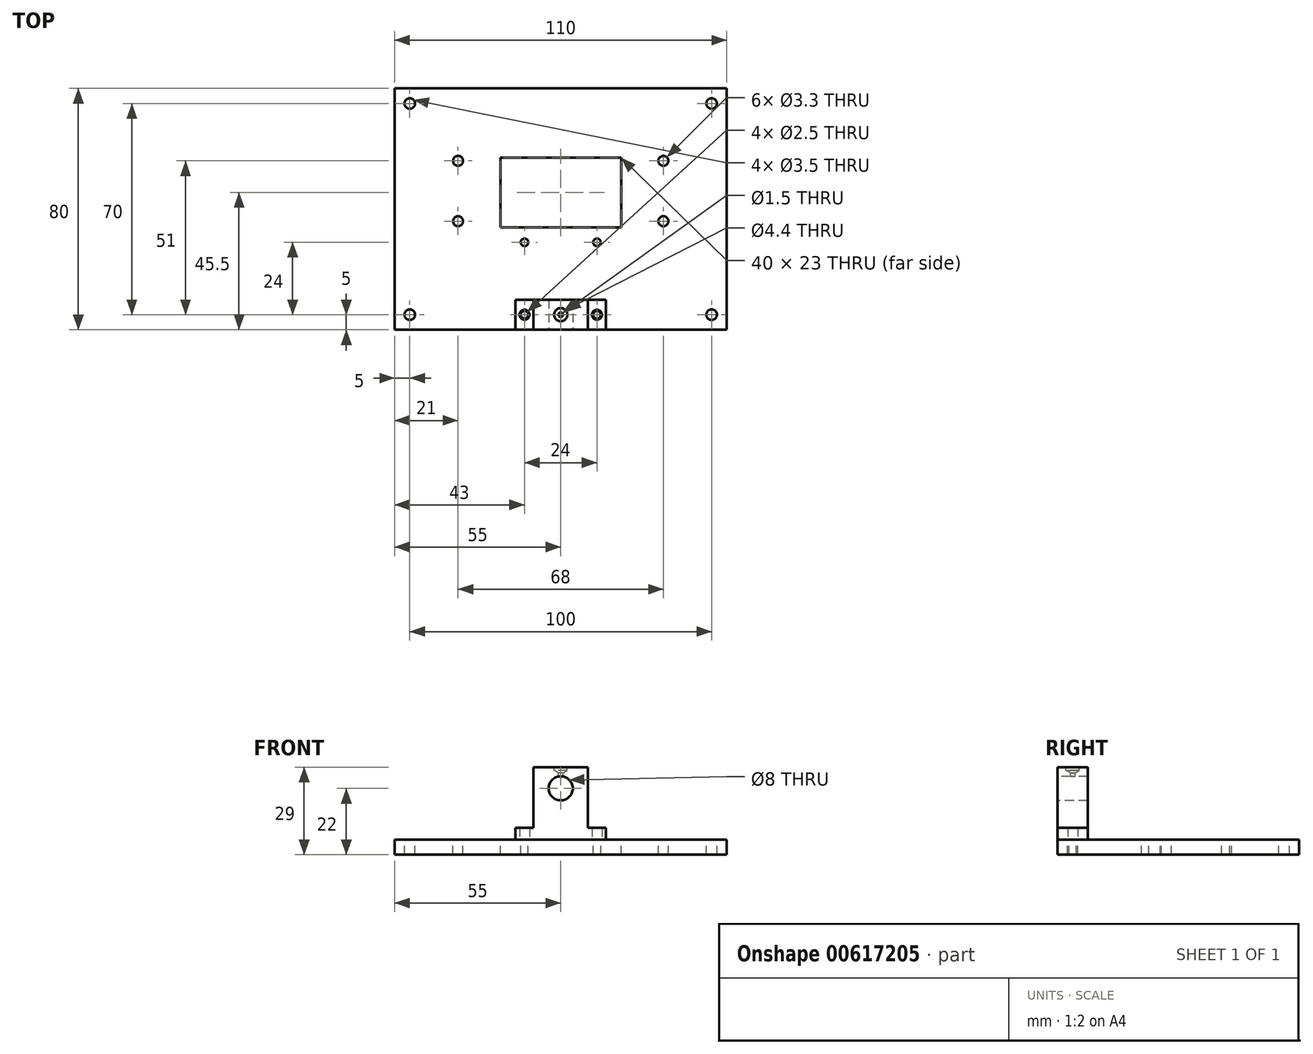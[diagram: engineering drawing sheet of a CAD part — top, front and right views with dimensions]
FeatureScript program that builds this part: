
annotation { "Feature Type Name" : "Feature", "Feature Type Description" : "" }
export const myFeature = defineFeature(function(context is Context, id is Id, definition is map)
    precondition{}
    {
        {
            var Q0;
            Q0=qCreatedBy(makeId("Top.planeOp"),FACE);
            var sketch = newSketch(context, id + "F0", { "sketchPlane" : qUnion([Q0])});
            skLineSegment(sketch, "E0.bottom", {"start": v(-55, 80) * mm, "end": v(55, 80) * mm});
            skLineSegment(sketch, "E0.top", {"start": v(-55, 0) * mm, "end": v(55, 0) * mm});
            skLineSegment(sketch, "E0.left", {"start": v(-55, 80) * mm, "end": v(-55, 0) * mm});
            skLineSegment(sketch, "E0.right", {"start": v(55, 80) * mm, "end": v(55, 0) * mm});
            skSolve(sketch);
        }
        {
            var Q0;
            Q0 = qSketchRegion(id + "F0", true);
            extrude(context, id + "F1", {"entities" : qUnion([Q0]), "oppositeDirection" : true, "depth" : 5 * mm, "offsetDistance" : 25 * mm});
        }
        {
            var Q0;
            Q0=makeQuery(id+"F1.opExtrude","CAP_FACE",FACE,{"disambiguationData":[OSD([sQuery(id+"F0.wireOp",EDGE,"E0.bottom"),sQuery(id+"F0.wireOp",EDGE,"E0.top"),sQuery(id+"F0.wireOp",EDGE,"E0.left"),sQuery(id+"F0.wireOp",EDGE,"E0.right")])],"isStart":true});
            var sketch = newSketch(context, id + "F2", { "sketchPlane" : qUnion([Q0])});
            skLineSegment(sketch, "E1.bottom", {"start": v(20, 34) * mm, "end": v(-20, 34) * mm});
            skLineSegment(sketch, "E1.top", {"start": v(20, 57) * mm, "end": v(-20, 57) * mm});
            skLineSegment(sketch, "E1.left", {"start": v(20, 34) * mm, "end": v(20, 57) * mm});
            skLineSegment(sketch, "E1.right", {"start": v(-20, 34) * mm, "end": v(-20, 57) * mm});
            skPoint(sketch, "E1.middle", {"position": v(0, 45.5) * mm});
            skSolve(sketch);
        }
        {
            var Q0;
            Q0 = qSketchRegion(id + "F2", true);
            extrude(context, id + "F3", {"entities" : qUnion([Q0]), "operationType" : NewBodyOperationType.REMOVE, "endBound" : BoundingType.THROUGH_ALL, "oppositeDirection" : true, "depth" : 25 * mm, "offsetDistance" : 25 * mm});
        }
        {
            var Q0;
            Q0=makeQuery(id+"F1.opExtrude","CAP_FACE",FACE,{"disambiguationData":[OSD([sQuery(id+"F0.wireOp",EDGE,"E0.bottom"),sQuery(id+"F0.wireOp",EDGE,"E0.top"),sQuery(id+"F0.wireOp",EDGE,"E0.left"),sQuery(id+"F0.wireOp",EDGE,"E0.right")])],"isStart":true});
            var sketch = newSketch(context, id + "F4", { "sketchPlane" : qUnion([Q0])});
            skLineSegment(sketch, "E2.bottom", {"start": v(12, 5) * mm, "end": v(-12, 5) * mm, "construction": true});
            skLineSegment(sketch, "E2.top", {"start": v(12, 29) * mm, "end": v(-12, 29) * mm, "construction": true});
            skLineSegment(sketch, "E2.left", {"start": v(12, 5) * mm, "end": v(12, 29) * mm, "construction": true});
            skLineSegment(sketch, "E2.right", {"start": v(-12, 5) * mm, "end": v(-12, 29) * mm, "construction": true});
            skPoint(sketch, "E2.middle", {"position": v(0, 17) * mm});
            skLineSegment(sketch, "E3.bottom", {"start": v(34, 36) * mm, "end": v(-34, 36) * mm, "construction": true});
            skLineSegment(sketch, "E3.top", {"start": v(34, 56) * mm, "end": v(-34, 56) * mm, "construction": true});
            skLineSegment(sketch, "E3.left", {"start": v(34, 36) * mm, "end": v(34, 56) * mm, "construction": true});
            skLineSegment(sketch, "E3.right", {"start": v(-34, 36) * mm, "end": v(-34, 56) * mm, "construction": true});
            skPoint(sketch, "E3.middle", {"position": v(0, 46) * mm});
            skSolve(sketch);
        }
        {
            var Q0;
            Q0=sQuery(id+"F4.wireOp",VERTEX,"E2.right.start");
            var Q1;
            Q1=sQuery(id+"F4.wireOp",VERTEX,"E2.bottom.start");
            var Q2;
            Q2=sQuery(id+"F4.wireOp",VERTEX,"E2.left.end");
            var Q3;
            Q3=sQuery(id+"F4.wireOp",VERTEX,"E2.right.end");
            var Q4;
            Q4=makeQuery(id+"F1.opExtrude","SWEPT_BODY",BODY,{"disambiguationData":[OSD([sQuery(id+"F0.wireOp",EDGE,"E0.bottom"),sQuery(id+"F0.wireOp",EDGE,"E0.top"),sQuery(id+"F0.wireOp",EDGE,"E0.left"),sQuery(id+"F0.wireOp",EDGE,"E0.right")])]});
            hole(context, id + "F5", {"style" : HoleStyle.SIMPLE, "endStyle" : HoleEndStyle.THROUGH, "standardTappedOrClearance" : lookupTablePath({ "standard" : "ISO", "engagement" : "75%", "pitch" : "0.5 mm", "size" : "M3", "type" : "Tapped" }), "standardBlindInLast" : lookupTablePath({ "standard" : "ISO", "engagement" : "75%", "pitch" : "0.5 mm", "size" : "M3", "type" : "Tapped" }), "holeDiameter" : 2.5 * mm, "majorDiameter" : 3 * mm, "showTappedDepth" : true, "isTappedThrough" : true, "tappedDepth" : 12 * mm, "tapClearance" : 3, "locations" : qUnion([Q0, Q1, Q2, Q3]), "scope" : qUnion([Q4])});
        }
        {
            var Q0;
            Q0=sQuery(id+"F4.wireOp",VERTEX,"E3.right.start");
            var Q1;
            Q1=sQuery(id+"F4.wireOp",VERTEX,"E3.left.start");
            var Q2;
            Q2=sQuery(id+"F4.wireOp",VERTEX,"E3.left.end");
            var Q3;
            Q3=sQuery(id+"F4.wireOp",VERTEX,"E3.top.end");
            var Q4;
            Q4=makeQuery(id+"F1.opExtrude","SWEPT_BODY",BODY,{"disambiguationData":[OSD([sQuery(id+"F0.wireOp",EDGE,"E0.bottom"),sQuery(id+"F0.wireOp",EDGE,"E0.top"),sQuery(id+"F0.wireOp",EDGE,"E0.left"),sQuery(id+"F0.wireOp",EDGE,"E0.right")])]});
            hole(context, id + "F6", {"style" : HoleStyle.SIMPLE, "endStyle" : HoleEndStyle.THROUGH, "standardTappedOrClearance" : lookupTablePath({ "standard" : "ISO", "engagement" : "75%", "pitch" : "0.7 mm", "size" : "M4", "type" : "Tapped" }), "standardBlindInLast" : lookupTablePath({ "standard" : "ISO", "engagement" : "75%", "pitch" : "0.7 mm", "size" : "M4", "type" : "Tapped" }), "holeDiameter" : 3.3 * mm, "majorDiameter" : 4 * mm, "showTappedDepth" : true, "isTappedThrough" : true, "tappedDepth" : 12 * mm, "tapClearance" : 3, "locations" : qUnion([Q0, Q1, Q2, Q3]), "scope" : qUnion([Q4])});
        }
        {
            var Q0;
            Q0=makeQuery(id+"F1.opExtrude","CAP_FACE",FACE,{"disambiguationData":[OSD([sQuery(id+"F0.wireOp",EDGE,"E0.bottom"),sQuery(id+"F0.wireOp",EDGE,"E0.top"),sQuery(id+"F0.wireOp",EDGE,"E0.left"),sQuery(id+"F0.wireOp",EDGE,"E0.right")])],"isStart":true});
            var sketch = newSketch(context, id + "F7", { "sketchPlane" : qUnion([Q0])});
            skLineSegment(sketch, "E4.bottom", {"start": v(50, 75) * mm, "end": v(-50, 75) * mm, "construction": true});
            skLineSegment(sketch, "E4.top", {"start": v(50, 5) * mm, "end": v(-50, 5) * mm, "construction": true});
            skLineSegment(sketch, "E4.left", {"start": v(50, 75) * mm, "end": v(50, 5) * mm, "construction": true});
            skLineSegment(sketch, "E4.right", {"start": v(-50, 75) * mm, "end": v(-50, 5) * mm, "construction": true});
            skPoint(sketch, "E4.middle", {"position": v(0, 40) * mm});
            skSolve(sketch);
        }
        {
            var Q0;
            Q0=sQuery(id+"F7.wireOp",VERTEX,"E4.right.end");
            var Q1;
            Q1=sQuery(id+"F7.wireOp",VERTEX,"E4.left.end");
            var Q2;
            Q2=sQuery(id+"F7.wireOp",VERTEX,"E4.left.start");
            var Q3;
            Q3=sQuery(id+"F7.wireOp",VERTEX,"E4.right.start");
            var Q4;
            Q4=makeQuery(id+"F1.opExtrude","SWEPT_BODY",BODY,{"disambiguationData":[OSD([sQuery(id+"F0.wireOp",EDGE,"E0.bottom"),sQuery(id+"F0.wireOp",EDGE,"E0.top"),sQuery(id+"F0.wireOp",EDGE,"E0.left"),sQuery(id+"F0.wireOp",EDGE,"E0.right")])]});
            hole(context, id + "F8", {"style" : HoleStyle.SIMPLE, "endStyle" : HoleEndStyle.THROUGH, "holeDiameter" : 3.5 * mm, "majorDiameter" : 4 * mm, "isTappedThrough" : true, "tappedDepth" : 12 * mm, "tapClearance" : 3, "locations" : qUnion([Q0, Q1, Q2, Q3]), "scope" : qUnion([Q4])});
        }
        {
            var Q0;
            Q0=makeQuery(id+"F1.opExtrude","CAP_FACE",FACE,{"disambiguationData":[OSD([sQuery(id+"F0.wireOp",EDGE,"E0.bottom"),sQuery(id+"F0.wireOp",EDGE,"E0.top"),sQuery(id+"F0.wireOp",EDGE,"E0.left"),sQuery(id+"F0.wireOp",EDGE,"E0.right")])],"isStart":true});
            var sketch = newSketch(context, id + "F9", { "sketchPlane" : qUnion([Q0])});
            skLineSegment(sketch, "E5.bottom", {"start": v(15, 0) * mm, "end": v(-15, 0) * mm});
            skLineSegment(sketch, "E5.top", {"start": v(15, 10) * mm, "end": v(-15, 10) * mm});
            skLineSegment(sketch, "E5.left", {"start": v(15, 0) * mm, "end": v(15, 10) * mm});
            skLineSegment(sketch, "E5.right", {"start": v(-15, 0) * mm, "end": v(-15, 10) * mm});
            skPoint(sketch, "E5.middle", {"position": v(0, 5) * mm});
            skLineSegment(sketch, "E6", {"start": v(-12, 5) * mm, "end": v(12, 5) * mm, "construction": true});
            skSolve(sketch);
        }
        {
            var Q0;
            Q0 = qSketchRegion(id + "F9", true);
            extrude(context, id + "F10", {"entities" : qUnion([Q0]), "depth" : 24 * mm, "offsetDistance" : 25 * mm});
        }
        {
            var Q0;
            Q0=makeQuery(id+"F10.opExtrude","SWEPT_FACE",FACE,{"disambiguationData":[OSD([sQuery(id+"F9.wireOp",EDGE,"E5.bottom")])]});
            var sketch = newSketch(context, id + "F11", { "sketchPlane" : qUnion([Q0])});
            skLineSegment(sketch, "E7", {"start": v(0, 0) * mm, "end": v(0, 24) * mm, "construction": true});
            skLineSegment(sketch, "E8.bottom", {"start": v(15, 24) * mm, "end": v(9, 24) * mm});
            skLineSegment(sketch, "E8.top", {"start": v(15, 4) * mm, "end": v(9, 4) * mm});
            skLineSegment(sketch, "E8.left", {"start": v(15, 24) * mm, "end": v(15, 4) * mm});
            skLineSegment(sketch, "E8.right", {"start": v(9, 24) * mm, "end": v(9, 4) * mm});
            skLineSegment(sketch, "E9.MirrorCS", {"start": v(-15, 4) * mm, "end": v(-9, 4) * mm});
            skLineSegment(sketch, "E10.MirrorCS", {"start": v(-9, 24) * mm, "end": v(-9, 4) * mm});
            skLineSegment(sketch, "E11.MirrorCS", {"start": v(-15, 24) * mm, "end": v(-15, 4) * mm});
            skLineSegment(sketch, "E12.MirrorCS", {"start": v(-15, 24) * mm, "end": v(-9, 24) * mm});
            skPoint(sketch, "E13", {"position": v(0, 17) * mm});
            skSolve(sketch);
        }
        {
            var Q0;
            Q0 = qSketchRegion(id + "F11", true);
            extrude(context, id + "F12", {"entities" : qUnion([Q0]), "operationType" : NewBodyOperationType.REMOVE, "endBound" : BoundingType.THROUGH_ALL, "oppositeDirection" : true, "depth" : 25 * mm, "offsetDistance" : 25 * mm});
        }
        {
            var Q0;
            Q0=sQuery(id+"F4.wireOp",VERTEX,"E2.right.start");
            var Q1;
            Q1=sQuery(id+"F4.wireOp",VERTEX,"E2.left.start");
            var Q2;
            Q2=makeQuery(id+"F10.opExtrude","SWEPT_BODY",BODY,{"disambiguationData":[OSD([sQuery(id+"F9.wireOp",EDGE,"E5.bottom"),sQuery(id+"F9.wireOp",EDGE,"E5.top"),sQuery(id+"F9.wireOp",EDGE,"E5.left"),sQuery(id+"F9.wireOp",EDGE,"E5.right")])]});
            hole(context, id + "F13", {"style" : HoleStyle.SIMPLE, "endStyle" : HoleEndStyle.THROUGH, "oppositeDirection" : true, "standardTappedOrClearance" : lookupTablePath({ "standard" : "ISO", "fit" : "Normal", "size" : "M3", "type" : "Clearance" }), "standardBlindInLast" : lookupTablePath({ "fit" : "Standard", "standard" : "ISO", "size" : "M3", "type" : "Clearance" }), "holeDiameter" : 3.3 * mm, "majorDiameter" : 5 * mm, "isTappedThrough" : true, "tappedDepth" : 6 * mm, "tapClearance" : 2, "locations" : qUnion([Q0, Q1]), "scope" : qUnion([Q2])});
        }
        {
            var Q0;
            Q0=sQuery(id+"F11.wireOp",VERTEX,"E13");
            var Q1;
            Q1=makeQuery(id+"F10.opExtrude","SWEPT_BODY",BODY,{"disambiguationData":[OSD([sQuery(id+"F9.wireOp",EDGE,"E5.bottom"),sQuery(id+"F9.wireOp",EDGE,"E5.top"),sQuery(id+"F9.wireOp",EDGE,"E5.left"),sQuery(id+"F9.wireOp",EDGE,"E5.right")])]});
            hole(context, id + "F14", {"style" : HoleStyle.SIMPLE, "endStyle" : HoleEndStyle.THROUGH, "standardTappedOrClearance" : lookupTablePath({ "standard" : "ISO", "size" : "8", "type" : "Drilled" }), "standardBlindInLast" : lookupTablePath({ "standard" : "ISO", "size" : "8", "type" : "Drilled" }), "holeDiameter" : 8 * mm, "majorDiameter" : 5 * mm, "isTappedThrough" : true, "tappedDepth" : 6 * mm, "tapClearance" : 2, "locations" : qUnion([Q0]), "scope" : qUnion([Q1])});
        }
        {
            var Q0;
            Q0=makeQuery(id+"F10.opExtrude","CAP_FACE",FACE,{"disambiguationData":[OSD([sQuery(id+"F9.wireOp",EDGE,"E5.bottom"),sQuery(id+"F9.wireOp",EDGE,"E5.top"),sQuery(id+"F9.wireOp",EDGE,"E5.left"),sQuery(id+"F9.wireOp",EDGE,"E5.right")])],"isStart":false});
            var sketch = newSketch(context, id + "F15", { "sketchPlane" : qUnion([Q0])});
            skLineSegment(sketch, "E14", {"start": v(-9, 10) * mm, "end": v(9, 0) * mm, "construction": true});
            skPoint(sketch, "E15", {"position": v(0, 5) * mm});
            skSolve(sketch);
        }
        {
            var Q0;
            Q0=sQuery(id+"F15.wireOp",VERTEX,"E15");
            var Q1;
            Q1=makeQuery(id+"F10.opExtrude","SWEPT_BODY",BODY,{"disambiguationData":[OSD([sQuery(id+"F9.wireOp",EDGE,"E5.bottom"),sQuery(id+"F9.wireOp",EDGE,"E5.top"),sQuery(id+"F9.wireOp",EDGE,"E5.left"),sQuery(id+"F9.wireOp",EDGE,"E5.right")])]});
            hole(context, id + "F16", {"style" : HoleStyle.SIMPLE, "endStyle" : HoleEndStyle.BLIND, "standardTappedOrClearance" : lookupTablePath({ "standard" : "ISO", "size" : "1.5", "type" : "Drilled" }), "standardBlindInLast" : lookupTablePath({ "standard" : "ISO", "size" : "1.5", "type" : "Drilled" }), "holeDiameter" : 1.5 * mm, "majorDiameter" : 5 * mm, "holeDepth" : 7.5 * mm, "isTappedThrough" : true, "tappedDepth" : 6 * mm, "tapClearance" : 2, "locations" : qUnion([Q0]), "scope" : qUnion([Q1])});
        }
        {
            var Q0;
            Q0=sQuery(id+"F15.wireOp",VERTEX,"E15");
            var Q1;
            Q1=makeQuery(id+"F10.opExtrude","SWEPT_BODY",BODY,{"disambiguationData":[OSD([sQuery(id+"F9.wireOp",EDGE,"E5.bottom"),sQuery(id+"F9.wireOp",EDGE,"E5.top"),sQuery(id+"F9.wireOp",EDGE,"E5.left"),sQuery(id+"F9.wireOp",EDGE,"E5.right")])]});
            hole(context, id + "F17", {"style" : HoleStyle.SIMPLE, "endStyle" : HoleEndStyle.BLIND, "standardTappedOrClearance" : lookupTablePath({ "standard" : "ISO", "size" : "4.4", "type" : "Drilled" }), "standardBlindInLast" : lookupTablePath({ "standard" : "ISO", "size" : "4.4", "type" : "Drilled" }), "holeDiameter" : 4.4 * mm, "majorDiameter" : 5 * mm, "holeDepth" : 1 * mm, "isTappedThrough" : true, "tappedDepth" : 6 * mm, "tapClearance" : 2, "locations" : qUnion([Q0]), "scope" : qUnion([Q1])});
        }
    });
